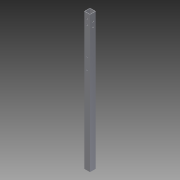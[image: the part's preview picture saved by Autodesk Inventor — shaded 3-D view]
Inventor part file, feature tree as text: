
AUTODESK INVENTOR PART (.ipt)
format: ipt  version: 2013 (Build 170138000, 138)  size: 100,864 bytes
history: native  units: in
note: dims shown in document units (in); Inventor stores cm internally (conversion verified against a paired STEP export)
features: extrude x4, sketch x4, reference x2
ambient origin geometry x8: Origin, YZ Plane, XZ Plane, XY Plane, X Axis, Y Axis, Z Axis, Center Point
bodies: Solid1 (feature_tree)
feature tree (10):
  extrude  "Extrusion1"  Depth=1.0in
  extrude  "Extrusion6"  Depth=23.5in TaperAngle=0.0deg
  extrude  "Extrusion7"  Depth=1.0in TaperAngle=0.0deg
  extrude  "Extrusion8"  [1 undecoded]
  sketch  "Sketch1"  dims[d0=1.0in d2=1.0in]
  sketch  "Sketch7"  dims[d3=0.0625in d4=23.5in d5=0.0in]
  sketch  "Sketch8"  dims[d18=1.0in d19=0.0in d20=1.0in d21=0.0in]
  sketch  "Sketch9"  dims[d22=1.0in d23=0.0in]
  reference  "Reference15"
  reference  "Reference16"
note: 1 required parameter value undecoded (feature->parameter linkage not recoverable at this tier; creation-order binding heuristic only, values carry confidence <= 0.55)
